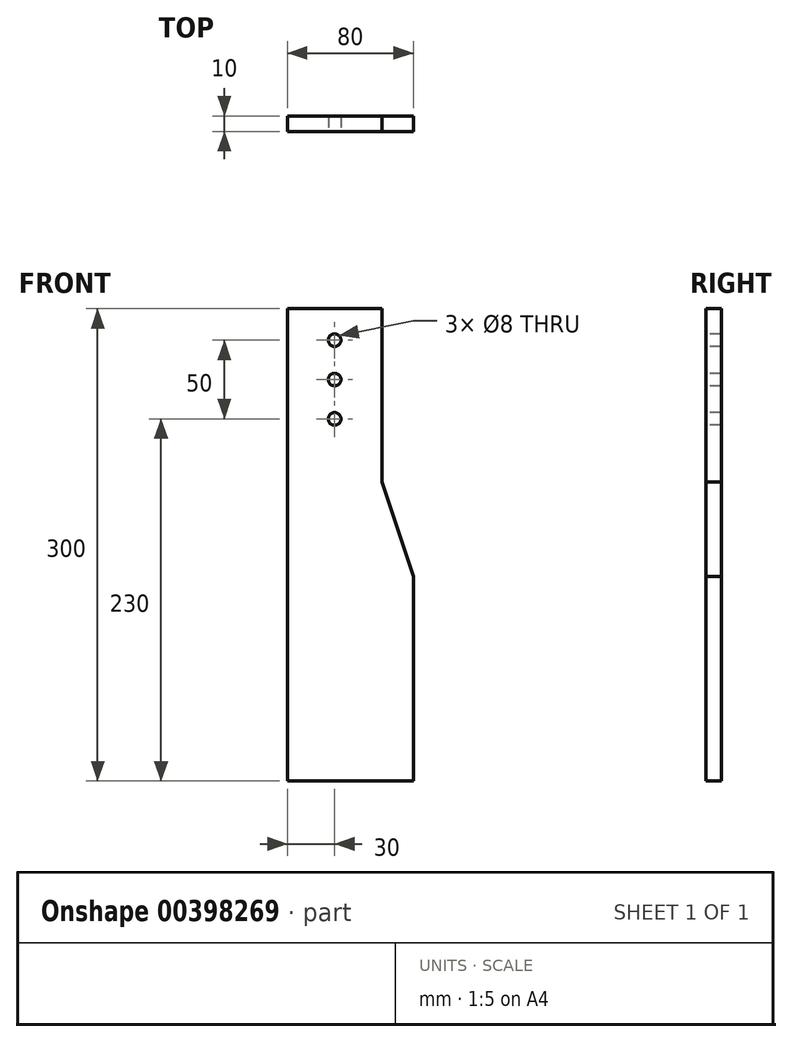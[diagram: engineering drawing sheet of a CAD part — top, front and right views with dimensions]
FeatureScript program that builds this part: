
annotation { "Feature Type Name" : "Feature", "Feature Type Description" : "" }
export const myFeature = defineFeature(function(context is Context, id is Id, definition is map)
    precondition{}
    {
        {
            var Q0;
            Q0=qCreatedBy(makeId("Front.planeOp"),FACE);
            var sketch = newSketch(context, id + "F0", { "sketchPlane" : qUnion([Q0])});
            skLineSegment(sketch, "E0", {"start": v(0, 0) * mm, "end": v(0, 300) * mm});
            skLineSegment(sketch, "E1", {"start": v(0, 300) * mm, "end": v(60, 300) * mm});
            skLineSegment(sketch, "E2", {"start": v(80, 130) * mm, "end": v(80, 0) * mm});
            skLineSegment(sketch, "E3", {"start": v(80, 0) * mm, "end": v(0, 0) * mm});
            skCircle(sketch, "E4", {"center": v(30, 280) * mm, "radius": 4 * mm});
            skCircle(sketch, "E5", {"center": v(30, 255) * mm, "radius": 4 * mm});
            skCircle(sketch, "E6", {"center": v(30, 230) * mm, "radius": 4 * mm});
            skLineSegment(sketch, "E7", {"start": v(30, 280) * mm, "end": v(30, 230) * mm, "construction": true});
            skLineSegment(sketch, "E8", {"start": v(60, 300) * mm, "end": v(60, 190) * mm});
            skLineSegment(sketch, "E9", {"start": v(60, 190) * mm, "end": v(80, 130) * mm});
            skSolve(sketch);
        }
        {
            var Q0;
            Q0 = qSketchRegion(id + "F0", true);
            extrude(context, id + "F1", {"entities" : qUnion([Q0]), "oppositeDirection" : true, "depth" : 10 * mm});
        }
    });
